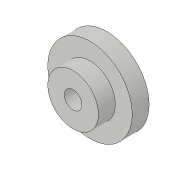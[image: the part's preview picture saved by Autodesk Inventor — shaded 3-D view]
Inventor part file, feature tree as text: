
AUTODESK INVENTOR PART (.ipt)
format: ipt  version: 2018.3 (Build 223284000, 284)  size: 92,672 bytes
history: native  units: in
note: dims shown in document units (in); Inventor stores cm internally (conversion verified against a paired STEP export)
features: extrude x2, sketch x2
ambient origin geometry x8: Origin, YZ Plane, XZ Plane, XY Plane, X Axis, Y Axis, Z Axis, Center Point
bodies: Body1 (feature_tree)
feature tree (4):
  extrude  "Extrusion4"  Depth=0.25in TaperAngle=0.0deg
  extrude  "Extrusion5"  Depth=0.125in TaperAngle=0.0deg
  sketch  "Sketch4"  dims[d9=0.13in d11=0.25in d12=0.0in]
  sketch  "Sketch5"  dims[d13=0.125in d14=0.125in d15=0.0in d16=0.374in]
